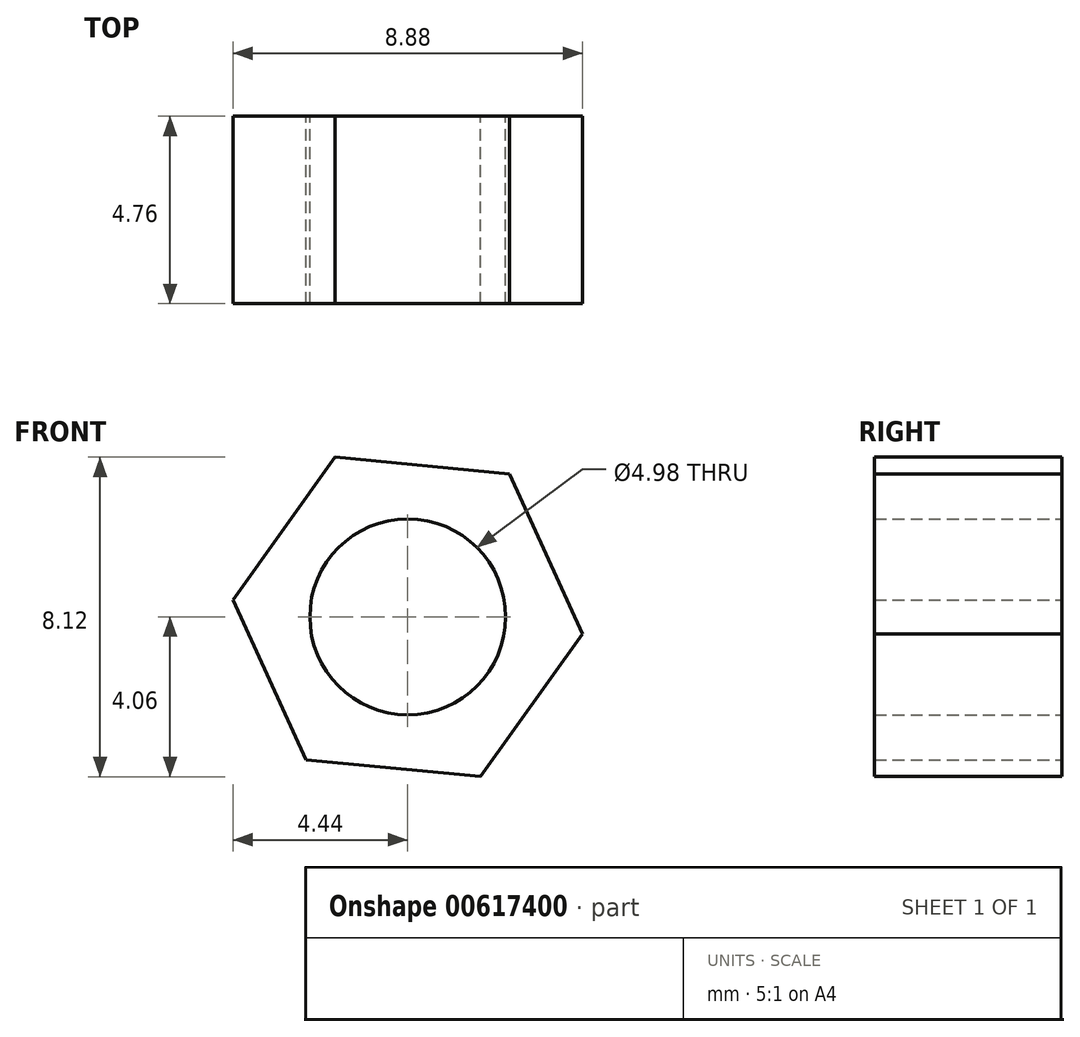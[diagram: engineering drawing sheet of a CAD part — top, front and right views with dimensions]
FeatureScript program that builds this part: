
annotation { "Feature Type Name" : "Feature", "Feature Type Description" : "" }
export const myFeature = defineFeature(function(context is Context, id is Id, definition is map)
    precondition{}
    {
        {
            var Q0;
            Q0=qCreatedBy(makeId("Front.planeOp"),FACE);
            var sketch = newSketch(context, id + "F0", { "sketchPlane" : qUnion([Q0])});
            skCircle(sketch, "E0", {"center": v(0, 0) * mm, "radius": 2.49 * mm});
            skCircle(sketch, "E1.cCircle", {"center": v(0, 0) * mm, "radius": 3.86 * mm, "construction": true});
            skLineSegment(sketch, "E1.0", {"start": v(2.59, 3.63) * mm, "end": v(4.44, -0.43) * mm});
            skLineSegment(sketch, "E1.1", {"start": v(4.44, -0.43) * mm, "end": v(1.85, -4.06) * mm});
            skLineSegment(sketch, "E1.2", {"start": v(1.85, -4.06) * mm, "end": v(-2.59, -3.63) * mm});
            skLineSegment(sketch, "E1.3", {"start": v(-2.59, -3.63) * mm, "end": v(-4.44, 0.43) * mm});
            skLineSegment(sketch, "E1.4", {"start": v(-4.44, 0.43) * mm, "end": v(-1.85, 4.06) * mm});
            skLineSegment(sketch, "E1.5", {"start": v(-1.85, 4.06) * mm, "end": v(2.59, 3.63) * mm});
            skPoint(sketch, "E1.0.midPoint", {"position": v(3.51, 1.6) * mm});
            skSolve(sketch);
        }
        {
            var Q0;
            Q0 = qSketchRegion(id + "F0", true);
            extrude(context, id + "F1", {"entities" : qUnion([Q0]), "depth" : 4.76 * mm, "offsetDistance" : 25.4 * mm});
        }
    });
